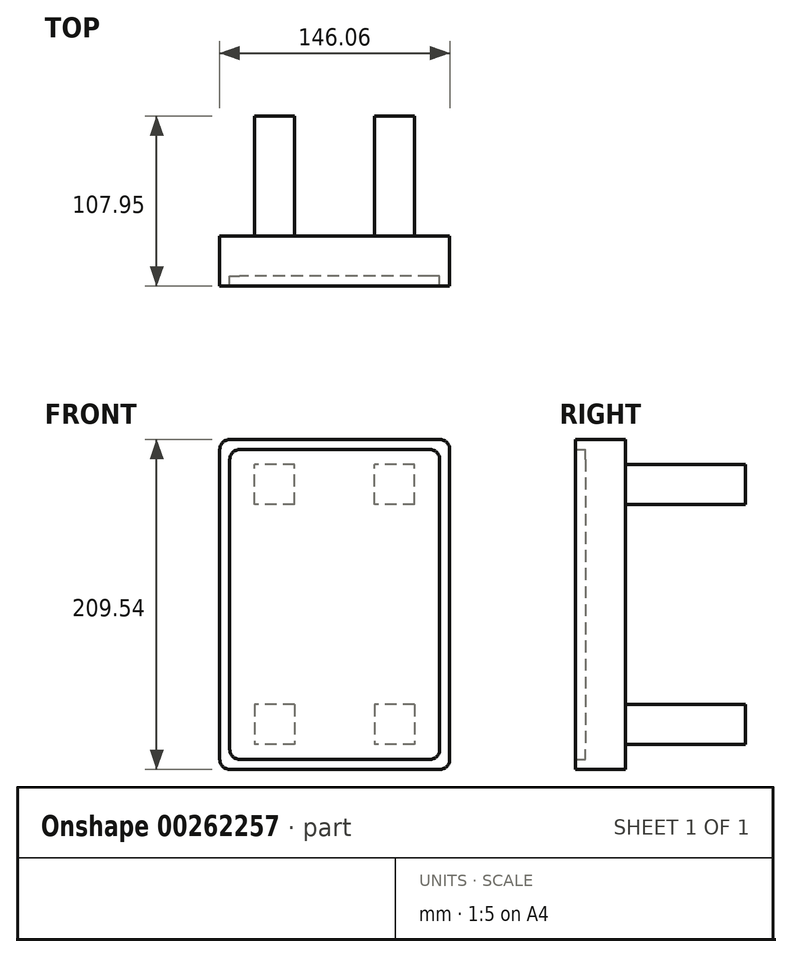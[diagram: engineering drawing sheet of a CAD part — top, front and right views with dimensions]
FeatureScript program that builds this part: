
annotation { "Feature Type Name" : "Feature", "Feature Type Description" : "" }
export const myFeature = defineFeature(function(context is Context, id is Id, definition is map)
    precondition{}
    {
        {
            var Q0;
            Q0=qCreatedBy(makeId("Front.planeOp"),FACE);
            var sketch = newSketch(context, id + "F0", { "sketchPlane" : qUnion([Q0])});
            skLineSegment(sketch, "E0", {"start": v(0, 0) * mm, "end": v(0, 76.2) * mm});
            skLineSegment(sketch, "E1", {"start": v(0, 0) * mm, "end": v(0, -76.2) * mm});
            skLineSegment(sketch, "E2", {"start": v(0, -76.2) * mm, "end": v(38.1, -76.2) * mm});
            skLineSegment(sketch, "E3", {"start": v(0, -76.2) * mm, "end": v(-38.1, -76.2) * mm});
            skLineSegment(sketch, "E4", {"start": v(0, 76.2) * mm, "end": v(38.1, 76.2) * mm});
            skLineSegment(sketch, "E5", {"start": v(0, 76.2) * mm, "end": v(-38.1, 76.2) * mm});
            skLineSegment(sketch, "E6.bottom", {"start": v(-25.4, 63.5) * mm, "end": v(-50.8, 63.5) * mm});
            skLineSegment(sketch, "E6.top", {"start": v(-25.4, 88.9) * mm, "end": v(-50.8, 88.9) * mm});
            skLineSegment(sketch, "E6.left", {"start": v(-25.4, 63.5) * mm, "end": v(-25.4, 88.9) * mm});
            skLineSegment(sketch, "E6.right", {"start": v(-50.8, 63.5) * mm, "end": v(-50.8, 88.9) * mm});
            skPoint(sketch, "E6.middle", {"position": v(-38.1, 76.2) * mm});
            skLineSegment(sketch, "E7.bottom", {"start": v(50.8, 63.5) * mm, "end": v(25.4, 63.5) * mm});
            skLineSegment(sketch, "E7.top", {"start": v(50.8, 88.9) * mm, "end": v(25.4, 88.9) * mm});
            skLineSegment(sketch, "E7.left", {"start": v(50.8, 63.5) * mm, "end": v(50.8, 88.9) * mm});
            skLineSegment(sketch, "E7.right", {"start": v(25.4, 63.5) * mm, "end": v(25.4, 88.9) * mm});
            skPoint(sketch, "E7.middle", {"position": v(38.1, 76.2) * mm});
            skLineSegment(sketch, "E8.bottom", {"start": v(50.8, -63.5) * mm, "end": v(25.4, -63.5) * mm});
            skLineSegment(sketch, "E8.top", {"start": v(50.8, -88.9) * mm, "end": v(25.4, -88.9) * mm});
            skLineSegment(sketch, "E8.left", {"start": v(50.8, -63.5) * mm, "end": v(50.8, -88.9) * mm});
            skLineSegment(sketch, "E8.right", {"start": v(25.4, -63.5) * mm, "end": v(25.4, -88.9) * mm});
            skPoint(sketch, "E8.middle", {"position": v(38.1, -76.2) * mm});
            skLineSegment(sketch, "E9.bottom", {"start": v(-25.4, -63.5) * mm, "end": v(-50.8, -63.5) * mm});
            skLineSegment(sketch, "E9.top", {"start": v(-25.4, -88.9) * mm, "end": v(-50.8, -88.9) * mm});
            skLineSegment(sketch, "E9.left", {"start": v(-25.4, -63.5) * mm, "end": v(-25.4, -88.9) * mm});
            skLineSegment(sketch, "E9.right", {"start": v(-50.8, -63.5) * mm, "end": v(-50.8, -88.9) * mm});
            skPoint(sketch, "E9.middle", {"position": v(-38.1, -76.2) * mm});
            skLineSegment(sketch, "E10.bottom", {"start": v(60.33, 98.43) * mm, "end": v(-60.33, 98.43) * mm});
            skLineSegment(sketch, "E10.top", {"start": v(60.33, -98.43) * mm, "end": v(-60.33, -98.43) * mm});
            skLineSegment(sketch, "E10.left", {"start": v(66.68, 92.08) * mm, "end": v(66.68, -92.08) * mm});
            skLineSegment(sketch, "E10.right", {"start": v(-66.68, 92.08) * mm, "end": v(-66.68, -92.08) * mm});
            skPoint(sketch, "E10.middle", {"position": v(0, 0) * mm});
            skPoint(sketch, "E11.visualSharp", {"position": v(-66.68, 98.43) * mm});
            skArc(sketch, "E11.filletArc", {"start": v(-60.33, 98.43) * mm, "mid": v(-64.82, 96.57) * mm, "end": v(-66.68, 92.08) * mm});
            skPoint(sketch, "E12.visualSharp", {"position": v(66.68, 98.43) * mm});
            skArc(sketch, "E12.filletArc", {"start": v(66.68, 92.08) * mm, "mid": v(64.82, 96.57) * mm, "end": v(60.33, 98.43) * mm});
            skPoint(sketch, "E13.visualSharp", {"position": v(66.68, -98.43) * mm});
            skArc(sketch, "E13.filletArc", {"start": v(60.33, -98.43) * mm, "mid": v(64.82, -96.57) * mm, "end": v(66.68, -92.08) * mm});
            skPoint(sketch, "E14.visualSharp", {"position": v(-66.68, -98.43) * mm});
            skArc(sketch, "E14.filletArc", {"start": v(-66.68, -92.08) * mm, "mid": v(-64.82, -96.57) * mm, "end": v(-60.33, -98.43) * mm});
            skLineSegment(sketch, "E15.bottom", {"start": v(-66.68, -104.78) * mm, "end": v(66.67, -104.78) * mm});
            skLineSegment(sketch, "E15.top", {"start": v(-66.67, 104.78) * mm, "end": v(66.67, 104.78) * mm});
            skLineSegment(sketch, "E15.left", {"start": v(-73.03, -98.43) * mm, "end": v(-73.03, 98.42) * mm});
            skLineSegment(sketch, "E15.right", {"start": v(73.03, -98.42) * mm, "end": v(73.03, 98.42) * mm});
            skPoint(sketch, "E16.visualSharp", {"position": v(-73.03, 104.78) * mm});
            skArc(sketch, "E16.filletArc", {"start": v(-66.67, 104.78) * mm, "mid": v(-71.17, 102.92) * mm, "end": v(-73.03, 98.42) * mm});
            skPoint(sketch, "E17.visualSharp", {"position": v(73.03, 104.78) * mm});
            skArc(sketch, "E17.filletArc", {"start": v(73.03, 98.42) * mm, "mid": v(71.17, 102.92) * mm, "end": v(66.67, 104.78) * mm});
            skPoint(sketch, "E18.visualSharp", {"position": v(73.03, -104.78) * mm});
            skArc(sketch, "E18.filletArc", {"start": v(66.67, -104.77) * mm, "mid": v(71.17, -102.92) * mm, "end": v(73.02, -98.42) * mm});
            skPoint(sketch, "E19.visualSharp", {"position": v(-73.03, -104.78) * mm});
            skArc(sketch, "E19.filletArc", {"start": v(-73.03, -98.43) * mm, "mid": v(-71.17, -102.92) * mm, "end": v(-66.68, -104.78) * mm});
            skSolve(sketch);
        }
        {
            var Q0;
            {var subQ3=sQuery(id+"F0.wireOp",EDGE,"E6.bottom");Q0=makeQuery(id+"F0.imprint","IMPRINT",FACE,{"disambiguationData":[TD([[makeQuery(id+"F0.imprint","IMPRINT",EDGE,{"derivedFrom":subQ3}),-1.0]])]});}
            var Q1;
            {var subQ1=sQuery(id+"F0.wireOp",EDGE,"E7.bottom");Q1=makeQuery(id+"F0.imprint","IMPRINT",FACE,{"disambiguationData":[TD([[makeQuery(id+"F0.imprint","IMPRINT",EDGE,{"derivedFrom":subQ1}),-1.0]])]});}
            var Q2;
            {var subQ14=sQuery(id+"F0.wireOp",EDGE,"E6.bottom");Q2=makeQuery(id+"F0.imprint","IMPRINT",FACE,{"disambiguationData":[TD([[makeQuery(id+"F0.imprint","IMPRINT",EDGE,{"derivedFrom":subQ14}),1.0]])]});}
            var Q3;
            {var subQ1=sQuery(id+"F0.wireOp",EDGE,"E8.bottom");Q3=makeQuery(id+"F0.imprint","IMPRINT",FACE,{"disambiguationData":[TD([[makeQuery(id+"F0.imprint","IMPRINT",EDGE,{"derivedFrom":subQ1}),1.0]])]});}
            var Q4;
            {var subQ3=sQuery(id+"F0.wireOp",EDGE,"E9.bottom");Q4=makeQuery(id+"F0.imprint","IMPRINT",FACE,{"disambiguationData":[TD([[makeQuery(id+"F0.imprint","IMPRINT",EDGE,{"derivedFrom":subQ3}),1.0]])]});}
            extrude(context, id + "F1", {"entities" : qUnion([Q0, Q1, Q2, Q3, Q4]), "depth" : 25.4 * mm});
        }
        {
            var Q0;
            Q0=makeQuery(id+"F0.imprint","IMPRINT",FACE,{"disambiguationData":[TD([[makeQuery(id+"F0.imprint","IMPRINT",EDGE,{"derivedFrom":sQuery(id+"F0.wireOp",EDGE,"E10.bottom")}),-1.0]])]});
            extrude(context, id + "F2", {"entities" : qUnion([Q0]), "operationType" : NewBodyOperationType.ADD, "depth" : 31.75 * mm});
        }
        {
            var Q0;
            {var subQ3=sQuery(id+"F0.wireOp",EDGE,"E6.bottom");Q0=makeQuery(id+"F0.imprint","IMPRINT",FACE,{"disambiguationData":[TD([[makeQuery(id+"F0.imprint","IMPRINT",EDGE,{"derivedFrom":subQ3}),-1.0]])]});}
            var Q1;
            {var subQ1=sQuery(id+"F0.wireOp",EDGE,"E7.bottom");Q1=makeQuery(id+"F0.imprint","IMPRINT",FACE,{"disambiguationData":[TD([[makeQuery(id+"F0.imprint","IMPRINT",EDGE,{"derivedFrom":subQ1}),-1.0]])]});}
            var Q2;
            {var subQ1=sQuery(id+"F0.wireOp",EDGE,"E8.bottom");Q2=makeQuery(id+"F0.imprint","IMPRINT",FACE,{"disambiguationData":[TD([[makeQuery(id+"F0.imprint","IMPRINT",EDGE,{"derivedFrom":subQ1}),1.0]])]});}
            var Q3;
            {var subQ3=sQuery(id+"F0.wireOp",EDGE,"E9.bottom");Q3=makeQuery(id+"F0.imprint","IMPRINT",FACE,{"disambiguationData":[TD([[makeQuery(id+"F0.imprint","IMPRINT",EDGE,{"derivedFrom":subQ3}),1.0]])]});}
            extrude(context, id + "F3", {"entities" : qUnion([Q0, Q1, Q2, Q3]), "oppositeDirection" : true, "depth" : 76.2 * mm});
        }
    });
